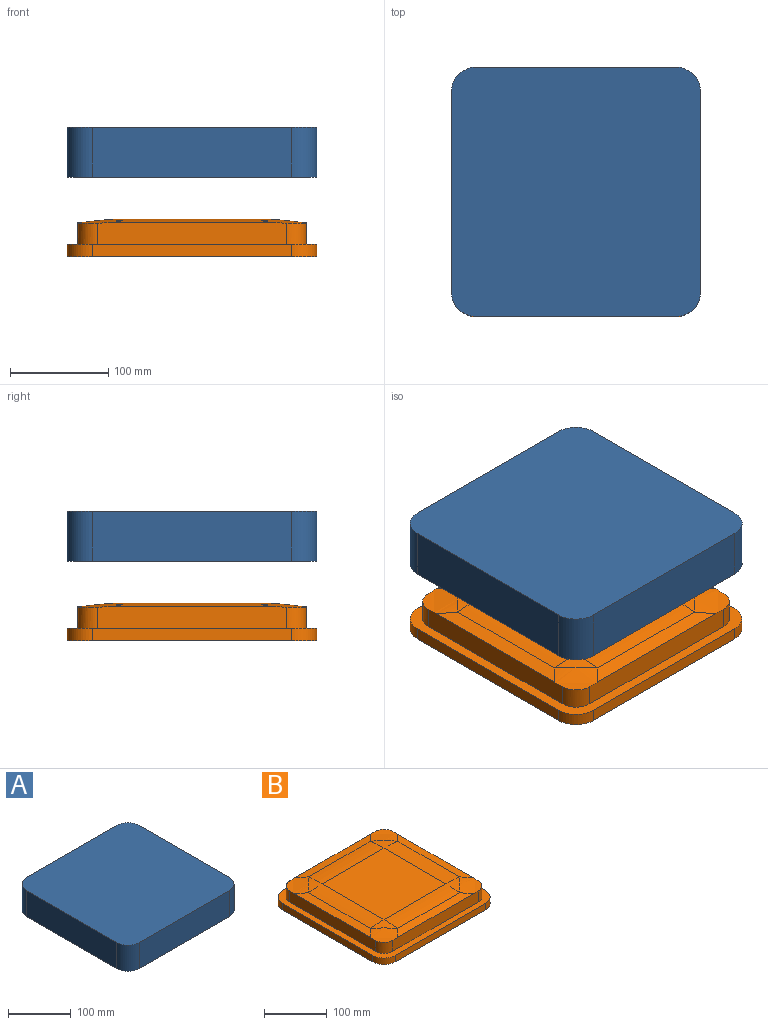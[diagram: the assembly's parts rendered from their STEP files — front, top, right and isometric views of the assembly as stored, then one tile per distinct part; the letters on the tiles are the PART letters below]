
ASSEMBLY  parts=2 mates=1
PART A: 76 faces, bbox 254.1x254.1x50.9 mm
  f0: plane 163.97x163.97mm, normal (0,0,-1), area 3443.1mm2, adj f9,f10,f11,f12,f13,f14,f15,f16
  f1: plane 174.87x23.83mm, normal (0,-0.34,-0.94), area 3756.2mm2, adj f5,f8,f9,f10,f11,f58
  f2: plane 174.87x23.83mm, normal (0.34,0,-0.94), area 3756.2mm2, adj f5,f6,f14,f16,f18,f50
  f3: plane 174.87x23.83mm, normal (0,0.34,-0.94), area 3756.2mm2, adj f6,f7,f22,f23,f24,f43
  f4: plane 174.87x23.83mm, normal (-0.34,0,-0.94), area 3756.2mm2, adj f7,f8,f15,f17,f19,f51
  f5: cylinder r=76.2mm len=56.54mm, axis (0.68,-0.68,0.25), area 1353.4mm2, adj f1,f2,f12,f52,f54,f56
  f6: cylinder r=76.2mm len=56.54mm, axis (0.68,0.68,0.25), area 1353.4mm2, adj f2,f3,f20,f44,f46,f48
  f7: cylinder r=76.2mm len=56.54mm, axis (-0.68,0.68,0.25), area 1353.4mm2, adj f3,f4,f21,f45,f47,f49
  f8: cylinder r=76.2mm len=56.54mm, axis (-0.68,-0.68,0.25), area 1353.4mm2, adj f1,f4,f13,f53,f55,f57
  f9: cylinder r=12.7mm len=111.77mm, axis (1,0,0), area 1589mm2, adj f0,f1,f10,f11
  f10: bspline ~17.19x10.65mm, area 95.6mm2, adj f0,f1,f9,f12
  f11: bspline ~17.19x10.65mm, area 95.6mm2, adj f0,f1,f9,f13
  f12: bspline ~27.87x27.87mm, area 487.7mm2, adj f0,f5,f10,f14
  f13: bspline ~27.87x27.87mm, area 487.7mm2, adj f0,f8,f11,f15
  f14: bspline ~10.64x8.69mm, area 95.6mm2, adj f0,f2,f12,f16
  f15: bspline ~10.64x8.69mm, area 95.6mm2, adj f0,f4,f13,f17
  f16: cylinder r=12.7mm len=111.77mm, axis (0,1,0), area 1589mm2, adj f0,f2,f14,f18
  f17: cylinder r=12.7mm len=111.77mm, axis (0,1,0), area 1589mm2, adj f0,f4,f15,f19
  f18: bspline ~10.64x8.69mm, area 95.6mm2, adj f0,f2,f16,f20
  f19: bspline ~10.64x8.69mm, area 95.6mm2, adj f0,f4,f17,f21
  f20: bspline ~27.87x27.87mm, area 487.7mm2, adj f0,f6,f18,f22
  f21: bspline ~27.87x27.87mm, area 487.7mm2, adj f0,f7,f19,f23
  f22: bspline ~10.64x8.69mm, area 95.6mm2, adj f0,f3,f20,f24
  f23: bspline ~10.64x8.69mm, area 95.6mm2, adj f0,f3,f21,f24
  f24: cylinder r=12.7mm len=111.77mm, axis (1,0,0), area 1589mm2, adj f0,f3,f22,f23
  f25: plane 181.56x21.84mm, normal (0,-1,0), area 3965.6mm2, adj f26,f32,f33,f56,f57,f58
  f26: extruded ~26.06x26.06mm, area 910.6mm2, adj f25,f27,f33,f54
  f27: plane 181.56x21.84mm, normal (1,0,0), area 3965.6mm2, adj f26,f28,f33,f48,f50,f52
  f28: extruded ~26.06x26.06mm, area 910.6mm2, adj f27,f29,f33,f46
  f29: plane 181.56x21.84mm, normal (0,1,0), area 3965.6mm2, adj f28,f30,f33,f43,f44,f45
  f30: extruded ~26.06x26.06mm, area 910.6mm2, adj f29,f31,f33,f47
  f31: plane 181.56x21.84mm, normal (-1,0,0), area 3965.6mm2, adj f30,f32,f33,f49,f51,f53
  f32: extruded ~26.06x26.06mm, area 910.6mm2, adj f25,f31,f33,f55
  f33: plane 254x254mm, normal (0,0,-1), area 9819.6mm2, adj f25,f26,f27,f28,f29,f30,f31,f32
  f34: plane 254x254mm, normal (0,0,1), area 63962.2mm2, adj f35,f36,f37,f38,f39,f40,f41,f42
  f35: plane 203.2x50.8mm, normal (0,-1,0), area 10322.6mm2, adj f33,f34,f36,f42
  f36: cylinder r=25.4mm len=50.8mm, axis (0,0,-1), area 2026.8mm2, adj f33,f34,f35,f37
  f37: plane 203.2x50.8mm, normal (1,0,0), area 10322.6mm2, adj f33,f34,f36,f38
  f38: cylinder r=25.4mm len=50.8mm, axis (0,0,-1), area 2026.8mm2, adj f33,f34,f37,f39
  f39: plane 203.2x50.8mm, normal (0,1,0), area 10322.6mm2, adj f33,f34,f38,f40
  f40: cylinder r=25.4mm len=50.8mm, axis (0,0,-1), area 2026.8mm2, adj f33,f34,f39,f41
  f41: plane 203.2x50.8mm, normal (-1,0,0), area 10322.6mm2, adj f33,f34,f40,f42
  f42: cylinder r=25.4mm len=50.8mm, axis (0,0,-1), area 2026.8mm2, adj f33,f34,f35,f41
  f43: cylinder r=5.08mm len=174.87mm, axis (-1,0,0), area 1085.3mm2, adj f3,f29,f44,f45
  f44: bspline ~4.83x3.48mm, area 21.4mm2, adj f6,f29,f43,f46
  f45: bspline ~4.83x3.48mm, area 21.4mm2, adj f7,f29,f43,f47
  f46: bspline ~28.5x27.69mm, area 262.4mm2, adj f6,f28,f44,f48
  f47: bspline ~28.5x27.69mm, area 262.4mm2, adj f7,f30,f45,f49
  f48: bspline ~4.83x3.48mm, area 21.4mm2, adj f6,f27,f46,f50
  f49: bspline ~4.83x3.48mm, area 21.4mm2, adj f7,f31,f47,f51
  f50: cylinder r=5.08mm len=174.87mm, axis (0,1,0), area 1085.3mm2, adj f2,f27,f48,f52
  f51: cylinder r=5.08mm len=174.87mm, axis (0,-1,0), area 1085.3mm2, adj f4,f31,f49,f53
  f52: bspline ~4.83x3.48mm, area 21.4mm2, adj f5,f27,f50,f54
  f53: bspline ~4.83x3.48mm, area 21.4mm2, adj f8,f31,f51,f55
  f54: bspline ~28.5x27.69mm, area 262.4mm2, adj f5,f26,f52,f56
  f55: bspline ~28.5x27.69mm, area 262.4mm2, adj f8,f32,f53,f57
  f56: bspline ~4.83x3.48mm, area 21.4mm2, adj f5,f25,f54,f58
  f57: bspline ~4.83x3.48mm, area 21.4mm2, adj f8,f25,f55,f58
  f58: cylinder r=5.08mm len=174.87mm, axis (1,0,0), area 1085.3mm2, adj f1,f25,f56,f57
  f59: cone r=17.78mm half-angle=10deg, axis (0,0,1), area 95.4mm2, adj f0,f60,f66,f70
  f60: plane 116.84x3.42mm, normal (0,0.98,-0.17), area 406mm2, adj f0,f59,f61,f72
  f61: cone r=17.78mm half-angle=10deg, axis (0,0,1), area 95.4mm2, adj f0,f60,f62,f74
  f62: plane 116.84x3.42mm, normal (0.98,0,-0.17), area 406mm2, adj f0,f61,f63,f75
  f63: cone r=17.78mm half-angle=10deg, axis (0,0,1), area 95.4mm2, adj f0,f62,f64,f73
  f64: plane 116.84x3.42mm, normal (0,-0.98,-0.17), area 406mm2, adj f0,f63,f65,f71
  f65: cone r=17.78mm half-angle=10deg, axis (0,0,1), area 95.4mm2, adj f0,f64,f66,f69
  f66: plane 116.84x3.42mm, normal (-0.98,0,-0.17), area 406mm2, adj f0,f59,f65,f68
  f67: plane 141.19x141.19mm, normal (0,0,-1), area 19806.7mm2, adj f68,f69,f70,f71,f72,f73,f74,f75
  f68: cylinder r=5.08mm len=116.84mm, axis (0,1,0), area 828.7mm2, adj f66,f67,f69,f70
  f69: torus R=12.17mm, axis (0,0,-1), area 169.1mm2, adj f65,f67,f68,f71
  f70: torus R=12.17mm, axis (0,0,-1), area 169.1mm2, adj f59,f67,f68,f72
  f71: cylinder r=5.08mm len=116.84mm, axis (1,0,0), area 828.7mm2, adj f64,f67,f69,f73
  f72: cylinder r=5.08mm len=116.84mm, axis (1,0,0), area 828.7mm2, adj f60,f67,f70,f74
  f73: torus R=12.17mm, axis (0,0,-1), area 169.1mm2, adj f63,f67,f71,f75
  f74: torus R=12.17mm, axis (0,0,-1), area 169.1mm2, adj f61,f67,f72,f75
  f75: cylinder r=5.08mm len=116.84mm, axis (0,1,0), area 828.7mm2, adj f62,f67,f73,f74
PART B: 40 faces, bbox 254x254x38.1 mm
  f0: plane 254x254mm, normal (0,0,1), area 10284.7mm2, adj f1,f2,f3,f4,f5,f6,f7,f8
  f1: cylinder r=25.4mm len=25.4mm, axis (0,0,-1), area 506.7mm2, adj f0,f2,f8,f34
  f2: plane 203.2x12.7mm, normal (0,-1,0), area 2580.6mm2, adj f0,f1,f3,f34
  f3: cylinder r=25.4mm len=25.4mm, axis (0,0,-1), area 506.7mm2, adj f0,f2,f4,f34
  f4: plane 203.2x12.7mm, normal (1,0,0), area 2580.6mm2, adj f0,f3,f5,f34
  f5: cylinder r=25.4mm len=25.4mm, axis (0,0,-1), area 506.7mm2, adj f0,f4,f6,f34
  f6: plane 203.2x12.7mm, normal (0,1,0), area 2580.6mm2, adj f0,f5,f7,f34
  f7: cylinder r=25.4mm len=25.4mm, axis (0,0,-1), area 506.7mm2, adj f0,f6,f8,f34
  f8: plane 203.2x12.7mm, normal (-1,0,0), area 2580.6mm2, adj f0,f1,f7,f34
  f9: cylinder r=19.81mm len=21.47mm, axis (0,0,-1), area 665.4mm2, adj f0,f10,f16,f33
  f10: plane 192.8x21.6mm, normal (0,-1,0), area 4161.3mm2, adj f0,f9,f11,f17,f27,f33
  f11: cylinder r=19.81mm len=21.47mm, axis (0,0,-1), area 665.4mm2, adj f0,f10,f12,f27
  f12: plane 192.8x21.6mm, normal (1,0,0), area 4161.3mm2, adj f0,f11,f13,f18,f22,f27
  f13: cylinder r=19.81mm len=21.47mm, axis (0,0,-1), area 665.4mm2, adj f0,f12,f14,f22
  f14: plane 192.8x21.6mm, normal (0,1,0), area 4161.3mm2, adj f0,f13,f15,f19,f22,f24
  f15: cylinder r=19.81mm len=21.47mm, axis (0,0,-1), area 665.4mm2, adj f0,f14,f16,f24
  f16: plane 192.8x21.6mm, normal (-1,0,0), area 4161.3mm2, adj f0,f9,f15,f20,f24,f33
  f17: plane 170.5x15.61mm, normal (0,-0.12,0.99), area 2436.1mm2, adj f10,f27,f31,f33
  f18: plane 170.5x15.61mm, normal (0.12,0,0.99), area 2436.1mm2, adj f12,f22,f26,f27
  f19: plane 170.5x15.61mm, normal (0,0.12,0.99), area 2436.1mm2, adj f14,f22,f24,f25
  f20: plane 170.5x15.61mm, normal (-0.12,0,0.99), area 2436.1mm2, adj f16,f24,f30,f33
  f21: plane 139.28x139.28mm, normal (0,0,1), area 19398.8mm2, adj f25,f26,f30,f31
  f22: cylinder r=254mm len=56.18mm, axis (0.7,0.7,-0.09), area 1365.6mm2, adj f12,f13,f14,f18,f19,f23
  f23: sphere r=254mm, area 482.7mm2, adj f22,f25,f26
  f24: cylinder r=254mm len=56.18mm, axis (-0.7,0.7,-0.09), area 1365.6mm2, adj f14,f15,f16,f19,f20,f28
  f25: cylinder r=254mm len=139.28mm, axis (1,0,0), area 4322.1mm2, adj f19,f21,f23,f28
  f26: cylinder r=254mm len=139.28mm, axis (0,-1,0), area 4322.1mm2, adj f18,f21,f23,f29
  f27: cylinder r=254mm len=56.18mm, axis (0.7,-0.7,-0.09), area 1365.6mm2, adj f10,f11,f12,f17,f18,f29
  f28: sphere r=254mm, area 482.7mm2, adj f24,f25,f30
  f29: sphere r=254mm, area 482.7mm2, adj f26,f27,f31
  f30: cylinder r=254mm len=139.28mm, axis (0,-1,0), area 4322.1mm2, adj f20,f21,f28,f32
  f31: cylinder r=254mm len=139.28mm, axis (1,0,0), area 4322.1mm2, adj f17,f21,f29,f32
  f32: sphere r=254mm, area 482.7mm2, adj f30,f31,f33
  f33: cylinder r=254mm len=56.18mm, axis (-0.7,-0.7,-0.09), area 1365.6mm2, adj f9,f10,f16,f17,f20,f32
  f34: plane 254x254mm, normal (0,0,-1), area 22671.9mm2, adj f1,f2,f3,f4,f5,f6,f7,f8
  f35: plane 203.2x25.4mm, normal (1,0,0), area 5161.3mm2, adj f34,f36,f38,f39
  f36: plane 203.2x25.4mm, normal (0,-1,0), area 5161.3mm2, adj f34,f35,f37,f39
  f37: plane 203.2x25.4mm, normal (-1,0,0), area 5161.3mm2, adj f34,f36,f38,f39
  f38: plane 203.2x25.4mm, normal (0,1,0), area 5161.3mm2, adj f34,f35,f37,f39
  f39: plane 203.2x203.2mm, normal (0,0,-1), area 41290.2mm2, adj f35,f36,f37,f38
PLACE A t=(-46.48,-71.05,-143.99)mm
PLACE B t=(130.47,-168.84,-262.94)mm
MATE slider A.f36 <-> B.f3  axis (0,0,-1) through (156.68,-166.22,-143.99)mm
